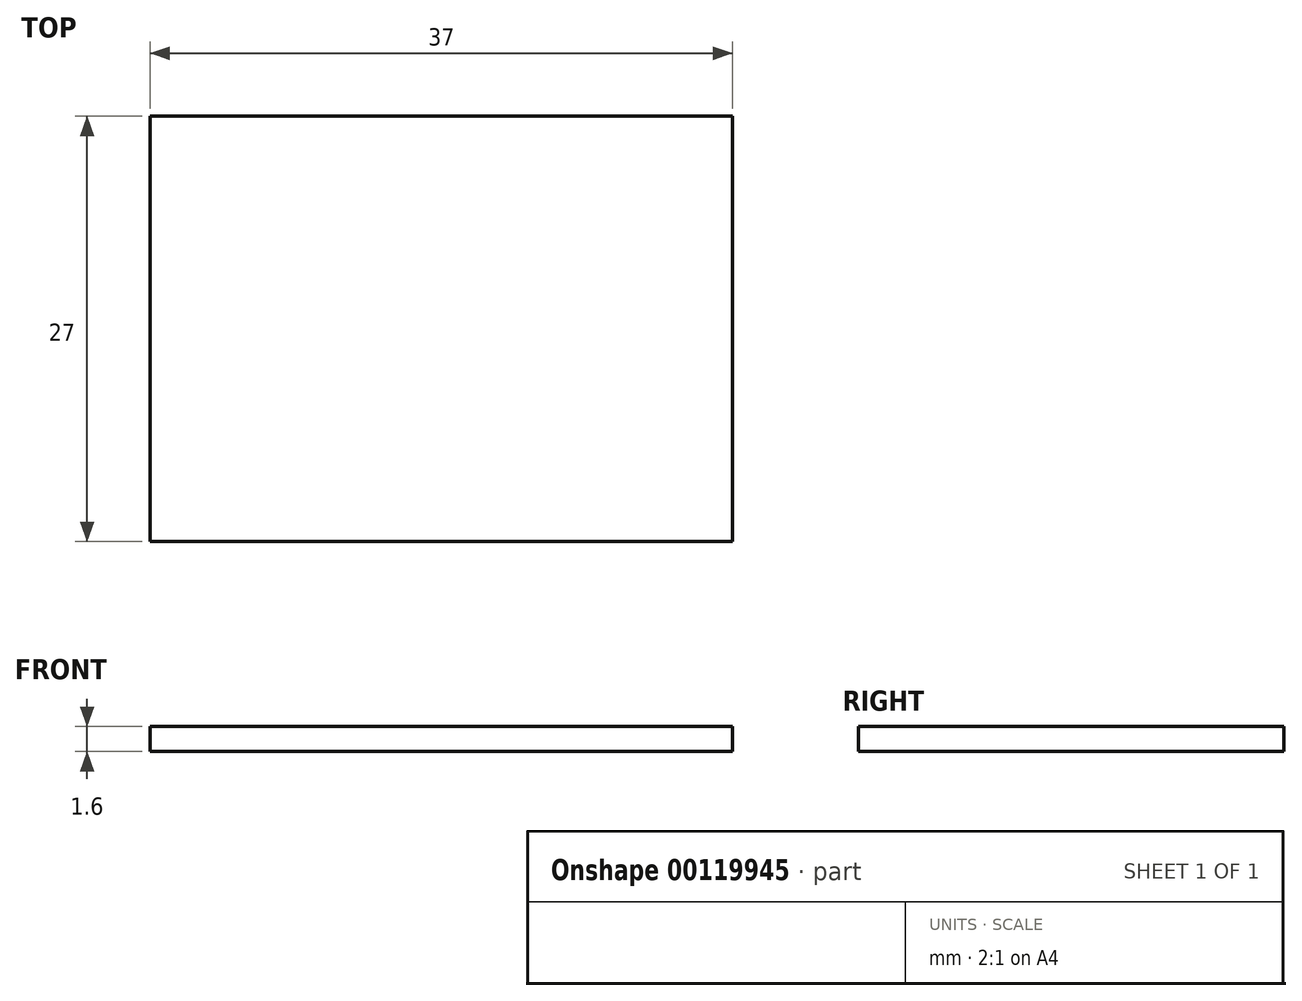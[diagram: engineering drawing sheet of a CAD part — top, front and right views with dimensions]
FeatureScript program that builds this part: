
annotation { "Feature Type Name" : "Feature", "Feature Type Description" : "" }
export const myFeature = defineFeature(function(context is Context, id is Id, definition is map)
    precondition{}
    {
        {
            var Q0;
            Q0=qCreatedBy(makeId("Top.planeOp"),FACE);
            var sketch = newSketch(context, id + "F0", { "sketchPlane" : qUnion([Q0])});
            skLineSegment(sketch, "E0.bottom", {"start": v(18.5, 13.5) * mm, "end": v(-18.5, 13.5) * mm});
            skLineSegment(sketch, "E0.top", {"start": v(18.5, -13.5) * mm, "end": v(-18.5, -13.5) * mm});
            skLineSegment(sketch, "E0.left", {"start": v(18.5, 13.5) * mm, "end": v(18.5, -13.5) * mm});
            skLineSegment(sketch, "E0.right", {"start": v(-18.5, 13.5) * mm, "end": v(-18.5, -13.5) * mm});
            skPoint(sketch, "E0.middle", {"position": v(0, 0) * mm});
            skSolve(sketch);
        }
        {
            var Q0;
            Q0=makeQuery(id+"F0.imprint","IMPRINT",FACE,{"disambiguationData":[TD([[makeQuery(id+"F0.imprint","IMPRINT",EDGE,{"derivedFrom":sQuery(id+"F0.wireOp",EDGE,"E0.bottom")}),1.0]])]});
            extrude(context, id + "F1", {"entities" : qUnion([Q0]), "depth" : 1.6 * mm});
        }
    });
